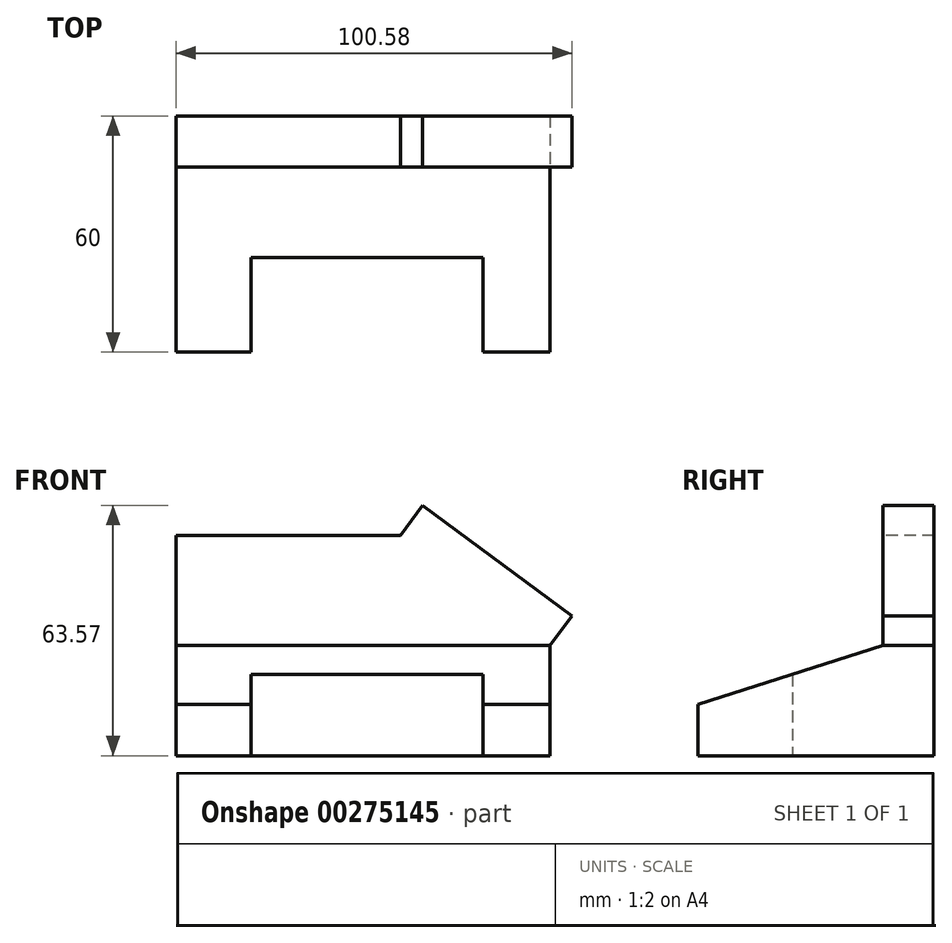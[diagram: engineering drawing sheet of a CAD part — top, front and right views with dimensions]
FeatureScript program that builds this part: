
annotation { "Feature Type Name" : "Feature", "Feature Type Description" : "" }
export const myFeature = defineFeature(function(context is Context, id is Id, definition is map)
    precondition{}
    {
        {
            var Q0;
            Q0=qCreatedBy(makeId("Right.planeOp"),FACE);
            var sketch = newSketch(context, id + "F0", { "sketchPlane" : qUnion([Q0])});
            skLineSegment(sketch, "E0", {"start": v(-60, 0) * mm, "end": v(0, 0) * mm});
            skLineSegment(sketch, "E1", {"start": v(0, 0) * mm, "end": v(0, 56) * mm});
            skLineSegment(sketch, "E2", {"start": v(-13, 28) * mm, "end": v(-13, 56) * mm});
            skLineSegment(sketch, "E3", {"start": v(-13, 56) * mm, "end": v(0, 56) * mm});
            skLineSegment(sketch, "E4", {"start": v(-60, 0) * mm, "end": v(-60, 13) * mm});
            skLineSegment(sketch, "E5", {"start": v(-60, 13) * mm, "end": v(-13, 28) * mm});
            skSolve(sketch);
        }
        {
            var Q0;
            Q0 = qSketchRegion(id + "F0", true);
            var Q1;
            Q1 = qSketchRegion(id + "F2", true);
            extrude(context, id + "F1", {"entities" : qUnion([Q0, Q1]), "depth" : 95 * mm});
        }
        {
            var Q0;
            Q0=makeQuery(id+"F1.opExtrude","SWEPT_FACE",FACE,{"disambiguationData":[OSD([sQuery(id+"F0.wireOp",EDGE,"E2")])]});
            var sketch = newSketch(context, id + "F2", { "sketchPlane" : qUnion([Q0])});
            skLineSegment(sketch, "E6", {"start": v(57, 56) * mm, "end": v(95, 28) * mm});
            skLineSegment(sketch, "E7", {"start": v(57, 56) * mm, "end": v(95, 56) * mm});
            skLineSegment(sketch, "E8", {"start": v(95, 56) * mm, "end": v(95, 28) * mm});
            skSolve(sketch);
        }
        {
            var Q0;
            Q0 = qSketchRegion(id + "F2", true);
            extrude(context, id + "F3", {"entities" : qUnion([Q0]), "operationType" : NewBodyOperationType.REMOVE, "endBound" : BoundingType.THROUGH_ALL, "oppositeDirection" : true, "depth" : 53 * mm});
        }
        {
            var Q0;
            Q0=makeQuery(id+"F1.opExtrude","SWEPT_FACE",FACE,{"disambiguationData":[OSD([sQuery(id+"F0.wireOp",EDGE,"E0")])]});
            var sketch = newSketch(context, id + "F4", { "sketchPlane" : qUnion([Q0])});
            skLineSegment(sketch, "E9.bottom", {"start": v(19, 60) * mm, "end": v(78, 60) * mm});
            skLineSegment(sketch, "E9.top", {"start": v(19, 36) * mm, "end": v(78, 36) * mm});
            skLineSegment(sketch, "E9.left", {"start": v(19, 60) * mm, "end": v(19, 36) * mm});
            skLineSegment(sketch, "E9.right", {"start": v(78, 60) * mm, "end": v(78, 36) * mm});
            skSolve(sketch);
        }
        {
            var Q0;
            Q0 = qSketchRegion(id + "F4", true);
            extrude(context, id + "F5", {"entities" : qUnion([Q0]), "operationType" : NewBodyOperationType.REMOVE, "endBound" : BoundingType.THROUGH_ALL, "oppositeDirection" : true, "depth" : 25 * mm});
        }
        {
            var Q0;
            Q0=makeQuery(id+"F3.boolean.opBoolean","COPY",FACE,{"derivedFrom":makeQuery(id+"F3.opExtrude","SWEPT_FACE",FACE,{"disambiguationData":[OSD([sQuery(id+"F2.wireOp",EDGE,"E6")])]})});
            extrude(context, id + "F6", {"entities" : qUnion([Q0]), "operationType" : NewBodyOperationType.ADD, "depth" : 9.4 * mm});
        }
    });
